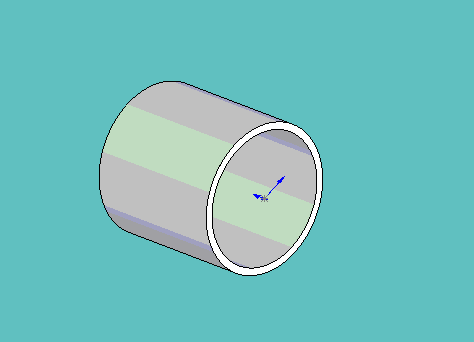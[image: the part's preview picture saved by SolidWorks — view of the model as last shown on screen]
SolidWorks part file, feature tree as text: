
SOLIDWORKS PART (.sldprt)
format: sldprt  version: not decoded by parser v0  size: 240,128 bytes
history: native  units: mm
features: sketch x3, cut_extrude x2, material x1, extrude x1 (+11 scaffold rows collapsed)
feature tree (18):
  scaffold x11  (default folders/planes/origin — collapsed)
  material  "Material <not specified>"
  sketch  "Sketch1"  dims[D1=1.5875mm D2=8.001mm D3=~0.396875mm]
  extrude  "Extrude1"  Depth=7.874mm
  sketch  "Sketch2"  dims[D1=~0.396875mm]
  cut_extrude  "Cut-Extrude1"  Depth=7.366mm
  sketch  "Sketch3"  dims[D1=4.7625mm]
  cut_extrude  "Cut-Extrude2"  [1 undecoded]
decode coverage: 5 of 6 modeling features carry decoded parameters
note: ~ marks probable driven/reference dimensions
note: 1 parameter value undecoded
note: suppression state not decoded; provenance and decode notes live in map.json
